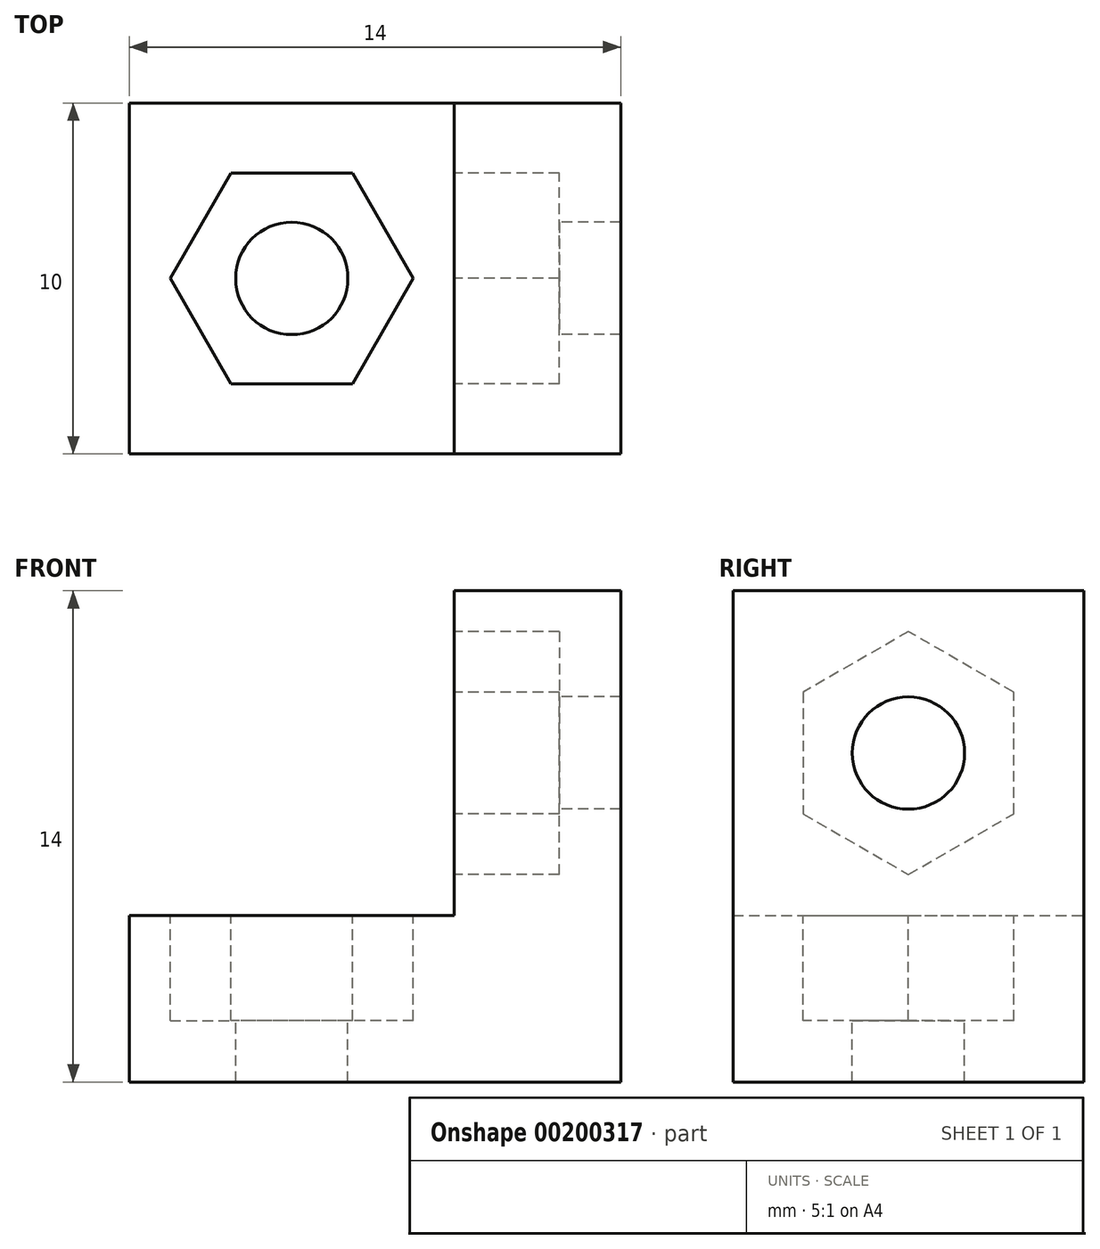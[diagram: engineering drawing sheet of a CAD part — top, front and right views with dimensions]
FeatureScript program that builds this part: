
annotation { "Feature Type Name" : "Feature", "Feature Type Description" : "" }
export const myFeature = defineFeature(function(context is Context, id is Id, definition is map)
    precondition{}
    {
        {
            var Q0;
            Q0=qCreatedBy(makeId("Front.planeOp"),FACE);
            var sketch = newSketch(context, id + "F0", { "sketchPlane" : qUnion([Q0])});
            skLineSegment(sketch, "E0", {"start": v(0, 0) * mm, "end": v(-14, 0) * mm});
            skLineSegment(sketch, "E1", {"start": v(0, 0) * mm, "end": v(0, 14) * mm});
            skLineSegment(sketch, "E2.0", {"start": v(-4.75, 4.75) * mm, "end": v(-4.75, 14) * mm});
            skLineSegment(sketch, "E2.1", {"start": v(-4.75, 4.75) * mm, "end": v(-14, 4.75) * mm});
            skLineSegment(sketch, "E3", {"start": v(-14, 4.75) * mm, "end": v(-14, 0) * mm});
            skLineSegment(sketch, "E4", {"start": v(-4.75, 14) * mm, "end": v(0, 14) * mm});
            skSolve(sketch);
        }
        {
            var Q0;
            Q0=makeQuery(id+"F0.imprint","IMPRINT",FACE,{"disambiguationData":[TD([[makeQuery(id+"F0.imprint","IMPRINT",EDGE,{"derivedFrom":sQuery(id+"F0.wireOp",EDGE,"E0")}),-1.0]])]});
            extrude(context, id + "F1", {"entities" : qUnion([Q0]), "depth" : 10 * mm});
        }
        {
            var Q0;
            Q0=makeQuery(id+"F1.opExtrude","SWEPT_FACE",FACE,{"disambiguationData":[OSD([sQuery(id+"F0.wireOp",EDGE,"E2.0")])]});
            var sketch = newSketch(context, id + "F2", { "sketchPlane" : qUnion([Q0])});
            skLineSegment(sketch, "E5", {"start": v(10, 9.38) * mm, "end": v(0, 9.38) * mm, "construction": true});
            skLineSegment(sketch, "E6", {"start": v(5, 14) * mm, "end": v(5, 4.75) * mm, "construction": true});
            skCircle(sketch, "E7", {"center": v(5, 9.38) * mm, "radius": 3 * mm, "construction": true});
            skCircle(sketch, "E8", {"center": v(5, 9.38) * mm, "radius": 1.6 * mm});
            skLineSegment(sketch, "E9.0", {"start": v(2, 7.64) * mm, "end": v(2, 11.1) * mm});
            skLineSegment(sketch, "E9.1", {"start": v(2, 11.1) * mm, "end": v(5, 12.84) * mm});
            skLineSegment(sketch, "E9.2", {"start": v(5, 12.84) * mm, "end": v(8, 11.1) * mm});
            skLineSegment(sketch, "E9.3", {"start": v(8, 11.1) * mm, "end": v(8, 7.64) * mm});
            skLineSegment(sketch, "E9.4", {"start": v(8, 7.64) * mm, "end": v(5, 5.91) * mm});
            skLineSegment(sketch, "E9.5", {"start": v(5, 5.91) * mm, "end": v(2, 7.64) * mm});
            skPoint(sketch, "E9.0.midPoint", {"position": v(2, 9.38) * mm});
            skSolve(sketch);
        }
        {
            var Q0;
            Q0=makeQuery(id+"F2.imprint","IMPRINT",FACE,{"disambiguationData":[TD([[makeQuery(id+"F2.imprint","IMPRINT",EDGE,{"derivedFrom":sQuery(id+"F2.wireOp",EDGE,"E8")}),-1.0]])]});
            extrude(context, id + "F3", {"entities" : qUnion([Q0]), "operationType" : NewBodyOperationType.REMOVE, "oppositeDirection" : true, "depth" : 3 * mm});
        }
        {
            var Q0;
            Q0=makeQuery(id+"F3.boolean.opBoolean","SPLIT",FACE,{"disambiguationData":[TD([makeQuery(id+"F3.opExtrude","SWEPT_FACE",FACE,{"disambiguationData":[OSD([sQuery(id+"F2.wireOp",EDGE,"E8")])]})])],"derivedFrom":makeQuery(id+"F1.opExtrude","SWEPT_FACE",FACE,{"disambiguationData":[OSD([sQuery(id+"F0.wireOp",EDGE,"E2.0")])]})});
            extrude(context, id + "F4", {"entities" : qUnion([Q0]), "operationType" : NewBodyOperationType.REMOVE, "oppositeDirection" : true, "depth" : 25 * mm});
        }
        {
            var Q0;
            Q0=makeQuery(id+"F1.opExtrude","SWEPT_FACE",FACE,{"disambiguationData":[OSD([sQuery(id+"F0.wireOp",EDGE,"E2.1")])]});
            var sketch = newSketch(context, id + "F5", { "sketchPlane" : qUnion([Q0])});
            skLineSegment(sketch, "E10", {"start": v(-9.38, 0) * mm, "end": v(-9.37, -10) * mm, "construction": true});
            skCircle(sketch, "E11", {"center": v(-9.38, -5) * mm, "radius": 1.6 * mm});
            skCircle(sketch, "E12", {"center": v(-9.38, -5) * mm, "radius": 3 * mm, "construction": true});
            skLineSegment(sketch, "E13.0", {"start": v(-7.64, -8) * mm, "end": v(-11.1, -8) * mm});
            skLineSegment(sketch, "E13.1", {"start": v(-11.1, -8) * mm, "end": v(-12.84, -5) * mm});
            skLineSegment(sketch, "E13.2", {"start": v(-12.84, -5) * mm, "end": v(-11.1, -2) * mm});
            skLineSegment(sketch, "E13.3", {"start": v(-11.1, -2) * mm, "end": v(-7.64, -2) * mm});
            skLineSegment(sketch, "E13.4", {"start": v(-7.64, -2) * mm, "end": v(-5.91, -5) * mm});
            skLineSegment(sketch, "E13.5", {"start": v(-5.91, -5) * mm, "end": v(-7.64, -8) * mm});
            skPoint(sketch, "E13.0.midPoint", {"position": v(-9.38, -8) * mm});
            skSolve(sketch);
        }
        {
            var Q0;
            Q0=makeQuery(id+"F5.imprint","IMPRINT",FACE,{"disambiguationData":[TD([[makeQuery(id+"F5.imprint","IMPRINT",EDGE,{"derivedFrom":sQuery(id+"F5.wireOp",EDGE,"E11")}),-1.0]])]});
            extrude(context, id + "F6", {"entities" : qUnion([Q0]), "operationType" : NewBodyOperationType.REMOVE, "oppositeDirection" : true, "depth" : 3 * mm});
        }
        {
            var Q0;
            Q0=makeQuery(id+"F6.boolean.opBoolean","SPLIT",FACE,{"disambiguationData":[TD([makeQuery(id+"F6.opExtrude","SWEPT_FACE",FACE,{"disambiguationData":[OSD([sQuery(id+"F5.wireOp",EDGE,"E11")])]})])],"derivedFrom":makeQuery(id+"F1.opExtrude","SWEPT_FACE",FACE,{"disambiguationData":[OSD([sQuery(id+"F0.wireOp",EDGE,"E2.1")])]})});
            extrude(context, id + "F7", {"entities" : qUnion([Q0]), "operationType" : NewBodyOperationType.REMOVE, "oppositeDirection" : true, "depth" : 25 * mm});
        }
    });
